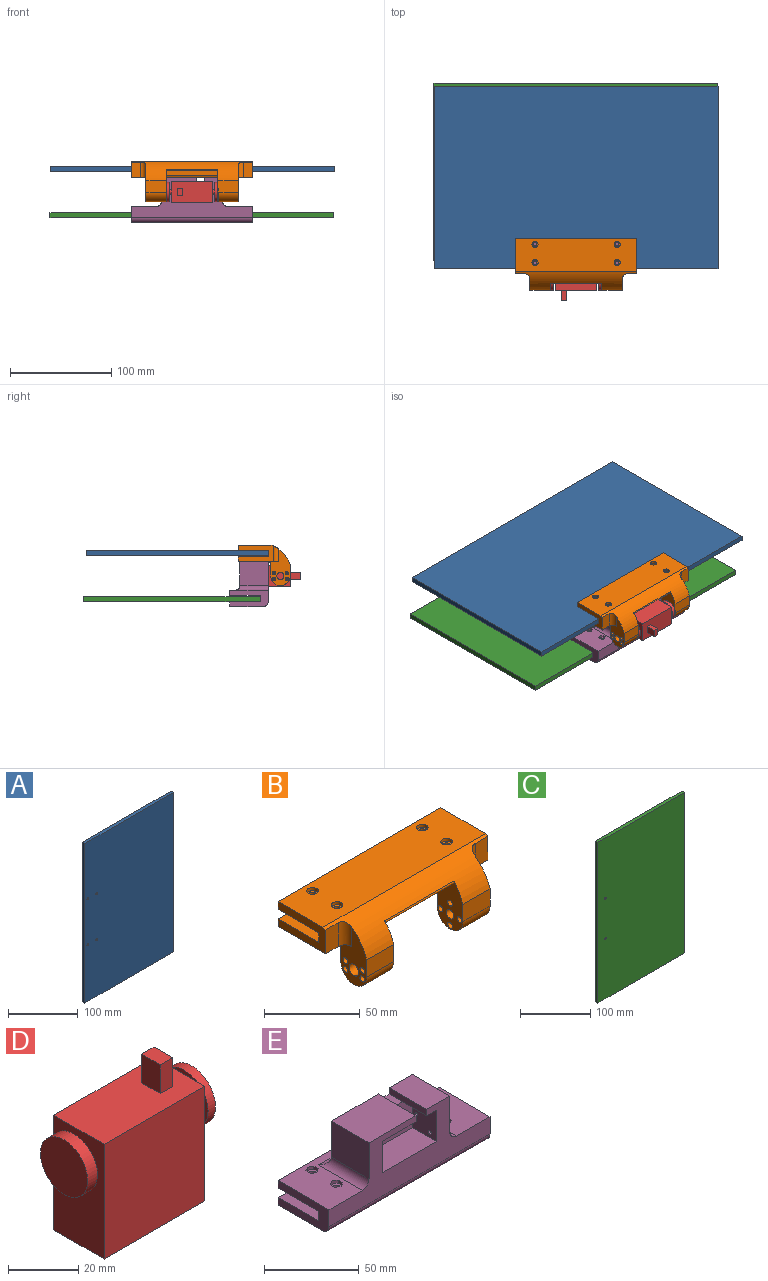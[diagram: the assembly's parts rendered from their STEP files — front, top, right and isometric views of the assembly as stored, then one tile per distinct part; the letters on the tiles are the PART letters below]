
ASSEMBLY  parts=5 mates=12
PART A: 10 faces, bbox 180x5x280 mm
  f0: plane 280x5mm, normal (1,0,0), area 1400mm2, adj f1,f6,f8,f9
  f1: plane 180x5mm, normal (0,0,1), area 900mm2, adj f0,f2,f8,f9
  f2: plane 280x5mm, normal (-1,0,0), area 1400mm2, adj f1,f6,f8,f9
  f3: cylinder r=1.75mm len=5mm, axis (0,1,0), area 55mm2, adj f8,f9
  f4: cylinder r=1.75mm len=5mm, axis (0,1,0), area 55mm2, adj f8,f9
  f5: cylinder r=1.75mm len=5mm, axis (0,1,0), area 55mm2, adj f8,f9
  f6: plane 180x5mm, normal (0,0,-1), area 900mm2, adj f0,f2,f8,f9
  f7: cylinder r=1.75mm len=5mm, axis (0,1,0), area 55mm2, adj f8,f9
  f8: plane 280x180mm, normal (0,-1,0), area 50361.5mm2, adj f0,f1,f2,f3,f4,f5,f6,f7
  f9: plane 280x180mm, normal (0,1,0), area 50361.5mm2, adj f0,f1,f2,f3,f4,f5,f6,f7
PART B: 92 faces, bbox 120x51x39.7 mm
  f0: plane 35.91x21mm, normal (-1,0,0), area 403.7mm2, adj f2,f12,f22,f28,f29,f33,f35,f37
  f1: plane 35.91x21mm, normal (1,0,0), area 418.5mm2, adj f2,f12,f21,f27,f30,f31,f42,f87
  f2: cylinder r=30mm len=120mm, axis (1,0,0), area 1848.5mm2, adj f0,f1,f11,f18,f19,f21,f28,f44
  f3: cylinder r=1.75mm len=3.5mm, axis (0,0,1), area 31.9mm2, adj f14,f76
  f4: cylinder r=1.75mm len=3.5mm, axis (0,0,1), area 31.9mm2, adj f14,f69
  f5: cylinder r=1.75mm len=3.5mm, axis (0,0,1), area 31.9mm2, adj f14,f68
  f6: cylinder r=1.75mm len=3.5mm, axis (0,0,1), area 31.9mm2, adj f14,f61
  f7: cylinder r=1.75mm len=3.5mm, axis (0,0,1), area 33mm2, adj f13,f53
  f8: cylinder r=1.75mm len=3.5mm, axis (0,0,1), area 33mm2, adj f13,f51
  f9: cylinder r=1.75mm len=3.5mm, axis (0,0,1), area 33mm2, adj f13,f50
  f10: cylinder r=1.75mm len=3.5mm, axis (0,0,1), area 33mm2, adj f13,f48
  f11: plane 120x33.17mm, normal (0,0,1), area 3867.3mm2, adj f2,f17,f44,f45,f47,f49,f52,f54
  f12: plane 120x40mm, normal (0,0,-1), area 3631mm2, adj f0,f1,f16,f42,f43,f44,f45,f55
  f13: plane 120x30mm, normal (0,0,-1), area 3561.5mm2, adj f7,f8,f9,f10,f15,f17,f44,f45
  f14: plane 120x30mm, normal (0,0,1), area 3561.5mm2, adj f3,f4,f5,f6,f15,f16,f44,f45
  f15: plane 120x6.1mm, normal (0,1,0), area 732mm2, adj f13,f14,f44,f45
  f16: plane 120x4.9mm, normal (0,1,0), area 588mm2, adj f12,f14,f44,f45
  f17: plane 120x5mm, normal (0,1,0), area 600mm2, adj f11,f13,f44,f45
  f18: plane 32.08x21mm, normal (1,0,0), area 467.1mm2, adj f2,f20,f22,f23,f24,f25,f26,f28
  f19: plane 32.08x21mm, normal (-1,0,0), area 457.2mm2, adj f2,f20,f21,f27,f30,f31,f41,f42
  f20: plane 51x11.57mm, normal (0,0,-1), area 589.9mm2, adj f18,f19,f41,f46
  f21: plane 20x10.9mm, normal (0,-1,0), area 218mm2, adj f1,f2,f19,f30
  f22: plane 20x12.15mm, normal (0,1,0), area 243mm2, adj f0,f18,f29,f43
  f23: cylinder r=1.05mm len=2.1mm, axis (1,0,0), area 9.9mm2, adj f18,f38
  f24: cylinder r=1.05mm len=2.1mm, axis (1,0,0), area 9.9mm2, adj f18,f36
  f25: cylinder r=1.05mm len=2.1mm, axis (1,0,0), area 9.9mm2, adj f18,f34
  f26: cylinder r=1.05mm len=2.1mm, axis (1,0,0), area 9.9mm2, adj f18,f32
  f27: plane 20x12.15mm, normal (0,1,0), area 243mm2, adj f1,f19,f30,f42
  f28: plane 20x10.9mm, normal (0,-1,0), area 218mm2, adj f0,f2,f18,f29
  f29: cylinder r=9.5mm len=20mm, axis (1,0,0), area 596.9mm2, adj f0,f18,f22,f28
  f30: cylinder r=9.5mm len=20mm, axis (1,0,0), area 596.9mm2, adj f1,f19,f21,f27
  f31: cylinder r=2.75mm len=20mm, axis (1,0,0), area 345.6mm2, adj f1,f19
  f32: plane 3.5x3.5mm, normal (-1,0,0), area 6.2mm2, adj f26,f33
  f33: cylinder r=1.75mm len=18.5mm, axis (-1,0,0), area 203.4mm2, adj f0,f32
  f34: plane 3.5x3.5mm, normal (-1,0,0), area 6.2mm2, adj f25,f35
  f35: cylinder r=1.75mm len=18.5mm, axis (-1,0,0), area 203.4mm2, adj f0,f34
  f36: plane 3.5x3.5mm, normal (-1,0,0), area 6.2mm2, adj f24,f37
  f37: cylinder r=1.75mm len=18.5mm, axis (-1,0,0), area 203.4mm2, adj f0,f36
  f38: plane 3.5x3.5mm, normal (-1,0,0), area 6.2mm2, adj f23,f39
  f39: cylinder r=1.75mm len=18.5mm, axis (-1,0,0), area 203.4mm2, adj f0,f38
  f40: cylinder r=3.5mm len=20mm, axis (-1,0,0), area 439.8mm2, adj f0,f18
  f41: plane 51x4.75mm, normal (0,-1,0), area 242.3mm2, adj f18,f19,f20,f83
  f42: cylinder r=2mm len=20mm, axis (-1,0,0), area 62.8mm2, adj f1,f12,f19,f27
  f43: cylinder r=2mm len=20mm, axis (-1,0,0), area 62.8mm2, adj f0,f12,f18,f22
  f44: plane 35x16mm, normal (1,0,0), area 376.3mm2, adj f2,f11,f12,f13,f14,f15,f16,f17
  f45: plane 35x16mm, normal (-1,0,0), area 376.3mm2, adj f2,f11,f12,f13,f14,f15,f16,f17
  f46: cylinder r=1mm len=51mm, axis (1,0,0), area 118.2mm2, adj f2,f18,f19,f20
  f47: cylinder r=3mm len=6mm, axis (0,0,1), area 37.7mm2, adj f11,f48
  f48: plane 6x6mm, normal (0,0,1), area 18.7mm2, adj f10,f47
  f49: cylinder r=3mm len=6mm, axis (0,0,1), area 37.7mm2, adj f11,f50
  f50: plane 6x6mm, normal (0,0,1), area 18.7mm2, adj f9,f49
  f51: plane 6x6mm, normal (0,0,1), area 18.7mm2, adj f8,f52
  f52: cylinder r=3mm len=6mm, axis (0,0,1), area 37.7mm2, adj f11,f51
  f53: plane 6x6mm, normal (0,0,1), area 18.7mm2, adj f7,f54
  f54: cylinder r=3mm len=6mm, axis (0,0,1), area 37.7mm2, adj f11,f53
  f55: plane 3x2mm, normal (-0.5,-0.87,0), area 6.9mm2, adj f12,f56,f60,f61
  f56: plane 3.46x2mm, normal (-1,0,0), area 6.9mm2, adj f12,f55,f57,f61
  f57: plane 3x2mm, normal (-0.5,0.87,0), area 6.9mm2, adj f12,f56,f58,f61
  f58: plane 3x2mm, normal (0.5,0.87,0), area 6.9mm2, adj f12,f57,f59,f61
  f59: plane 3.46x2mm, normal (1,0,0), area 6.9mm2, adj f12,f58,f60,f61
  f60: plane 3x2mm, normal (0.5,-0.87,0), area 6.9mm2, adj f12,f55,f59,f61
  f61: plane 6.93x6mm, normal (0,0,-1), area 21.6mm2, adj f6,f55,f56,f57,f58,f59,f60
  f62: plane 3x2mm, normal (-0.5,-0.87,0), area 6.9mm2, adj f12,f63,f67,f68
  f63: plane 3.46x2mm, normal (-1,0,0), area 6.9mm2, adj f12,f62,f64,f68
  f64: plane 3x2mm, normal (-0.5,0.87,0), area 6.9mm2, adj f12,f63,f65,f68
  f65: plane 3x2mm, normal (0.5,0.87,0), area 6.9mm2, adj f12,f64,f66,f68
  f66: plane 3.46x2mm, normal (1,0,0), area 6.9mm2, adj f12,f65,f67,f68
  f67: plane 3x2mm, normal (0.5,-0.87,0), area 6.9mm2, adj f12,f62,f66,f68
  f68: plane 6.93x6mm, normal (0,0,-1), area 21.6mm2, adj f5,f62,f63,f64,f65,f66,f67
  f69: plane 6.93x6mm, normal (0,0,-1), area 21.6mm2, adj f4,f70,f71,f72,f73,f74,f75
  f70: plane 3x2mm, normal (-0.5,-0.87,0), area 6.9mm2, adj f12,f69,f71,f75
  f71: plane 3.46x2mm, normal (-1,0,0), area 6.9mm2, adj f12,f69,f70,f72
  f72: plane 3x2mm, normal (-0.5,0.87,0), area 6.9mm2, adj f12,f69,f71,f73
  f73: plane 3x2mm, normal (0.5,0.87,0), area 6.9mm2, adj f12,f69,f72,f74
  f74: plane 3.46x2mm, normal (1,0,0), area 6.9mm2, adj f12,f69,f73,f75
  f75: plane 3x2mm, normal (0.5,-0.87,0), area 6.9mm2, adj f12,f69,f70,f74
  f76: plane 6.93x6mm, normal (0,0,-1), area 21.6mm2, adj f3,f77,f78,f79,f80,f81,f82
  f77: plane 3x2mm, normal (-0.5,-0.87,0), area 6.9mm2, adj f12,f76,f78,f82
  f78: plane 3.46x2mm, normal (-1,0,0), area 6.9mm2, adj f12,f76,f77,f79
  f79: plane 3x2mm, normal (-0.5,0.87,0), area 6.9mm2, adj f12,f76,f78,f80
  f80: plane 3x2mm, normal (0.5,0.87,0), area 6.9mm2, adj f12,f76,f79,f81
  f81: plane 3.46x2mm, normal (1,0,0), area 6.9mm2, adj f12,f76,f80,f82
  f82: plane 3x2mm, normal (0.5,-0.87,0), area 6.9mm2, adj f12,f76,f77,f81
  f83: cylinder r=2mm len=51mm, axis (-1,0,0), area 160.2mm2, adj f12,f18,f19,f41
  f84: plane 15.22x9.5mm, normal (0,-1,0), area 144.6mm2, adj f2,f12,f44,f87
  f85: plane 15.22x9.5mm, normal (0,-1,0), area 144.6mm2, adj f2,f12,f45,f86
  f86: cylinder r=5mm len=15.22mm, axis (0,0,1), area 111.8mm2, adj f0,f2,f12,f85
  f87: cylinder r=5mm len=15.22mm, axis (0,0,-1), area 111.8mm2, adj f1,f2,f12,f84
  f88: cylinder r=1.75mm len=20mm, axis (1,0,0), area 219.9mm2, adj f1,f19
  f89: cylinder r=1.75mm len=20mm, axis (1,0,0), area 219.9mm2, adj f1,f19
  f90: cylinder r=1.75mm len=20mm, axis (1,0,0), area 219.9mm2, adj f1,f19
  f91: cylinder r=1.75mm len=20mm, axis (1,0,0), area 219.9mm2, adj f1,f19
PART C: 8 faces, bbox 174.5x5x280 mm
  f0: plane 280x5mm, normal (1,0,0), area 1400mm2, adj f1,f4,f6,f7
  f1: plane 174.5x5mm, normal (0,0,1), area 872.5mm2, adj f0,f2,f6,f7
  f2: plane 280x5mm, normal (-1,0,0), area 1400mm2, adj f1,f4,f6,f7
  f3: cylinder r=1.5mm len=5mm, axis (0,1,0), area 47.1mm2, adj f6,f7
  f4: plane 174.5x5mm, normal (0,0,-1), area 872.5mm2, adj f0,f2,f6,f7
  f5: cylinder r=1.5mm len=5mm, axis (0,1,0), area 47.1mm2, adj f6,f7
  f6: plane 280x174.5mm, normal (0,-1,0), area 48845.9mm2, adj f0,f1,f2,f3,f4,f5
  f7: plane 280x174.5mm, normal (0,1,0), area 48845.9mm2, adj f0,f1,f2,f3,f4,f5
PART D: 19 faces, bbox 51.5x20.3x50 mm
  f0: plane 40.5x20.3mm, normal (0,0,1), area 784.7mm2, adj f1,f3,f4,f5,f14,f15,f16,f17
  f1: plane 40x20.3mm, normal (-1,0,0), area 792.4mm2, adj f0,f2,f4,f5,f6
  f2: plane 40.5x20.3mm, normal (0,0,-1), area 822.2mm2, adj f1,f3,f4,f5
  f3: plane 40x20.3mm, normal (1,0,0), area 792.4mm2, adj f0,f2,f4,f5,f7
  f4: plane 40.5x40mm, normal (0,-1,0), area 1620mm2, adj f0,f1,f2,f3
  f5: plane 40.5x40mm, normal (0,1,0), area 1620mm2, adj f0,f1,f2,f3
  f6: cylinder r=2.5mm len=5mm, axis (1,0,0), area 31.4mm2, adj f1,f10
  f7: cylinder r=2.5mm len=5mm, axis (-1,0,0), area 31.4mm2, adj f3,f13
  f8: cylinder r=9.5mm len=19mm, axis (1,0,0), area 238.8mm2, adj f9,f10
  f9: plane 19x19mm, normal (-1,0,0), area 283.5mm2, adj f8
  f10: plane 19x19mm, normal (1,0,0), area 263.9mm2, adj f6,f8
  f11: cylinder r=9.5mm len=19mm, axis (-1,0,0), area 179.1mm2, adj f12,f13
  f12: plane 19x19mm, normal (1,0,0), area 283.5mm2, adj f11
  f13: plane 19x19mm, normal (-1,0,0), area 263.9mm2, adj f7,f11
  f14: plane 10x5mm, normal (0,1,0), area 50mm2, adj f0,f15,f17,f18
  f15: plane 10x7.5mm, normal (-1,0,0), area 75mm2, adj f0,f14,f16,f18
  f16: plane 10x5mm, normal (0,-1,0), area 50mm2, adj f0,f15,f17,f18
  f17: plane 10x7.5mm, normal (1,0,0), area 75mm2, adj f0,f14,f16,f18
  f18: plane 7.5x5mm, normal (0,0,1), area 37.5mm2, adj f14,f15,f16,f17
PART E: 81 faces, bbox 120x38x44.3 mm
  f0: cylinder r=1.75mm len=3.5mm, axis (0,0,1), area 33mm2, adj f15,f71
  f1: cylinder r=1.75mm len=3.5mm, axis (0,0,1), area 33mm2, adj f15,f64
  f2: cylinder r=1.75mm len=3.5mm, axis (0,0,1), area 33mm2, adj f15,f63
  f3: cylinder r=1.75mm len=3.5mm, axis (0,0,1), area 33mm2, adj f15,f56
  f4: cylinder r=1.75mm len=3.5mm, axis (0,0,1), area 31.9mm2, adj f12,f48
  f5: cylinder r=1.75mm len=3.5mm, axis (0,0,1), area 31.9mm2, adj f12,f46
  f6: cylinder r=1.75mm len=3.5mm, axis (0,0,1), area 31.9mm2, adj f12,f45
  f7: cylinder r=1.75mm len=3.5mm, axis (0,0,1), area 31.9mm2, adj f12,f43
  f8: plane 120x33mm, normal (0,0,-1), area 3846.9mm2, adj f11,f39,f40,f41,f42,f44,f47,f49
  f9: plane 120x39.3mm, normal (0,-1,0), area 2187.1mm2, adj f10,f19,f20,f22,f23,f24,f25,f26
  f10: plane 120x38mm, normal (0,0,1), area 2115.4mm2, adj f9,f14,f39,f40,f50,f51,f52,f53
  f11: plane 120x4.9mm, normal (0,1,0), area 588mm2, adj f8,f12,f39,f40
  f12: plane 120x30mm, normal (0,0,1), area 3561.5mm2, adj f4,f5,f6,f7,f11,f13,f39,f40
  f13: plane 120x6.1mm, normal (0,1,0), area 732mm2, adj f12,f15,f39,f40
  f14: plane 120x5mm, normal (0,1,0), area 600mm2, adj f10,f15,f39,f40
  f15: plane 120x30mm, normal (0,0,-1), area 3561.5mm2, adj f0,f1,f2,f3,f13,f14,f39,f40
  f16: cylinder r=1.05mm len=2.1mm, axis (1,0,0), area 9.9mm2, adj f29,f37
  f17: cylinder r=1.05mm len=2.1mm, axis (1,0,0), area 9.9mm2, adj f29,f35
  f18: cylinder r=1.05mm len=2.1mm, axis (1,0,0), area 9.9mm2, adj f29,f33
  f19: plane 28x23.3mm, normal (-1,0,0), area 652.4mm2, adj f9,f21,f25,f78
  f20: plane 28x23.3mm, normal (1,0,0), area 623.5mm2, adj f9,f21,f26,f34,f36,f38,f79
  f21: plane 60.3x23.3mm, normal (0,1,0), area 1373mm2, adj f19,f20,f24,f25,f26,f27,f32,f80
  f22: plane 20.3x18mm, normal (1,0,0), area 365.4mm2, adj f9,f23,f30,f31
  f23: plane 25x18mm, normal (0,0,-1), area 450mm2, adj f9,f22,f24,f31
  f24: plane 28x4mm, normal (1,0,0), area 112mm2, adj f9,f21,f23,f25,f32
  f25: plane 35x28mm, normal (0,0,1), area 980mm2, adj f9,f19,f21,f24
  f26: plane 28x17.3mm, normal (0,0,1), area 484.4mm2, adj f9,f20,f21,f27
  f27: plane 28x4mm, normal (-1,0,0), area 112mm2, adj f9,f21,f26,f28,f32
  f28: plane 18x7.3mm, normal (0,0,-1), area 131.4mm2, adj f9,f27,f29,f31
  f29: plane 20.3x18mm, normal (-1,0,0), area 355mm2, adj f9,f16,f17,f18,f28,f30,f31
  f30: plane 40.3x18mm, normal (0,0,1), area 725.4mm2, adj f9,f22,f29,f31
  f31: plane 40.3x20.3mm, normal (0,-1,0), area 818.1mm2, adj f22,f23,f28,f29,f30,f32
  f32: plane 10x8mm, normal (0,0,1), area 80mm2, adj f21,f24,f27,f31
  f33: plane 3.5x3.5mm, normal (1,0,0), area 6.2mm2, adj f18,f34
  f34: cylinder r=1.75mm len=8.5mm, axis (1,0,0), area 93.5mm2, adj f20,f33
  f35: plane 3.5x3.5mm, normal (1,0,0), area 6.2mm2, adj f17,f36
  f36: cylinder r=1.75mm len=8.5mm, axis (1,0,0), area 93.5mm2, adj f20,f35
  f37: plane 3.5x3.5mm, normal (1,0,0), area 6.2mm2, adj f16,f38
  f38: cylinder r=1.75mm len=8.5mm, axis (1,0,0), area 93.5mm2, adj f20,f37
  f39: plane 38x16mm, normal (-1,0,0), area 419.6mm2, adj f8,f9,f10,f11,f12,f13,f14,f15
  f40: plane 38x16mm, normal (1,0,0), area 419.6mm2, adj f8,f9,f10,f11,f12,f13,f14,f15
  f41: cylinder r=5mm len=120mm, axis (-1,0,0), area 942.5mm2, adj f8,f9,f39,f40
  f42: cylinder r=3mm len=6mm, axis (0,0,-1), area 37.7mm2, adj f8,f43
  f43: plane 6x6mm, normal (0,0,-1), area 18.7mm2, adj f7,f42
  f44: cylinder r=3mm len=6mm, axis (0,0,-1), area 37.7mm2, adj f8,f45
  f45: plane 6x6mm, normal (0,0,-1), area 18.7mm2, adj f6,f44
  f46: plane 6x6mm, normal (0,0,-1), area 18.7mm2, adj f5,f47
  f47: cylinder r=3mm len=6mm, axis (0,0,-1), area 37.7mm2, adj f8,f46
  f48: plane 6x6mm, normal (0,0,-1), area 18.7mm2, adj f4,f49
  f49: cylinder r=3mm len=6mm, axis (0,0,-1), area 37.7mm2, adj f8,f48
  f50: plane 3x2mm, normal (0.5,-0.87,0), area 6.9mm2, adj f10,f51,f55,f56
  f51: plane 3.46x2mm, normal (1,0,0), area 6.9mm2, adj f10,f50,f52,f56
  f52: plane 3x2mm, normal (0.5,0.87,0), area 6.9mm2, adj f10,f51,f53,f56
  f53: plane 3x2mm, normal (-0.5,0.87,0), area 6.9mm2, adj f10,f52,f54,f56
  f54: plane 3.46x2mm, normal (-1,0,0), area 6.9mm2, adj f10,f53,f55,f56
  f55: plane 3x2mm, normal (-0.5,-0.87,0), area 6.9mm2, adj f10,f50,f54,f56
  f56: plane 6.93x6mm, normal (0,0,1), area 21.6mm2, adj f3,f50,f51,f52,f53,f54,f55
  f57: plane 3x2mm, normal (-0.5,0.87,0), area 6.9mm2, adj f10,f58,f62,f63
  f58: plane 3.46x2mm, normal (-1,0,0), area 6.9mm2, adj f10,f57,f59,f63
  f59: plane 3x2mm, normal (-0.5,-0.87,0), area 6.9mm2, adj f10,f58,f60,f63
  f60: plane 3x2mm, normal (0.5,-0.87,0), area 6.9mm2, adj f10,f59,f61,f63
  f61: plane 3.46x2mm, normal (1,0,0), area 6.9mm2, adj f10,f60,f62,f63
  f62: plane 3x2mm, normal (0.5,0.87,0), area 6.9mm2, adj f10,f57,f61,f63
  f63: plane 6.93x6mm, normal (0,0,1), area 21.6mm2, adj f2,f57,f58,f59,f60,f61,f62
  f64: plane 6.93x6mm, normal (0,0,1), area 21.6mm2, adj f1,f65,f66,f67,f68,f69,f70
  f65: plane 3x2mm, normal (0.5,-0.87,0), area 6.9mm2, adj f10,f64,f66,f70
  f66: plane 3.46x2mm, normal (1,0,0), area 6.9mm2, adj f10,f64,f65,f67
  f67: plane 3x2mm, normal (0.5,0.87,0), area 6.9mm2, adj f10,f64,f66,f68
  f68: plane 3x2mm, normal (-0.5,0.87,0), area 6.9mm2, adj f10,f64,f67,f69
  f69: plane 3.46x2mm, normal (-1,0,0), area 6.9mm2, adj f10,f64,f68,f70
  f70: plane 3x2mm, normal (-0.5,-0.87,0), area 6.9mm2, adj f10,f64,f65,f69
  f71: plane 6.93x6mm, normal (0,0,1), area 21.6mm2, adj f0,f72,f73,f74,f75,f76,f77
  f72: plane 3x2mm, normal (-0.5,0.87,0), area 6.9mm2, adj f10,f71,f73,f77
  f73: plane 3.46x2mm, normal (-1,0,0), area 6.9mm2, adj f10,f71,f72,f74
  f74: plane 3x2mm, normal (-0.5,-0.87,0), area 6.9mm2, adj f10,f71,f73,f75
  f75: plane 3x2mm, normal (0.5,-0.87,0), area 6.9mm2, adj f10,f71,f74,f76
  f76: plane 3.46x2mm, normal (1,0,0), area 6.9mm2, adj f10,f71,f75,f77
  f77: plane 3x2mm, normal (0.5,0.87,0), area 6.9mm2, adj f10,f71,f72,f76
  f78: cylinder r=5mm len=33mm, axis (0,-1,0), area 234.2mm2, adj f9,f10,f19,f80
  f79: cylinder r=5mm len=33mm, axis (0,1,0), area 234.2mm2, adj f9,f10,f20,f80
  f80: cylinder r=5mm len=70.3mm, axis (1,0,0), area 502.1mm2, adj f10,f21,f78,f79
PLACE A rot(axis=(-0.58,-0.58,0.58),120deg) t=(-61,47.58,-21.27)mm
PLACE B t=(-86.5,-44.42,-50.92)mm
PLACE C rot(axis=(-0.58,-0.58,0.58),120deg) t=(-61.15,53.33,-66.67)mm
PLACE D rot(axis=(0,-0.71,0.71),180deg) t=(-41,-23.92,-51.57)mm
PLACE E t=(-61.15,-23.92,-41.42)mm fixed
MATE planar D.f5 <-> E.f30  axis (0,0,-1) through (-61.25,-43.92,-51.57)mm
MATE cylindrical C.f3 <-> E.f1  axis (0,0,-1) through (-96.65,-18.92,-64.17)mm
MATE planar D.f1 <-> E.f29  axis (1,0,0) through (-41,-43.67,-41.42)mm
MATE parallel A.f8 <-> C.f6  axis (0,0,1) through (-61,47.64,-16.27)mm
MATE cylindrical D.f7 <-> B.f29  axis (1,0,0) through (-85,-53.92,-41.42)mm
MATE planar C.f7 <-> E.f12  axis (0,0,-1) through (-61.15,53.35,-66.67)mm
MATE planar D.f2 <-> E.f31  axis (0,1,0) through (-61.25,-23.92,-41.42)mm
MATE cylindrical A.f3 <-> B.f49  axis (0,0,-1) through (-20.5,-18.42,-21.27)mm
MATE cylindrical A.f5 <-> B.f54  axis (0,0,-1) through (-101.5,-36.42,-18.77)mm
MATE planar B.f13 <-> A.f8  axis (0,0,-1) through (-61,-27.42,-16.27)mm
MATE planar B.f18 <-> D.f7  axis (1,0,0) through (-86.5,-53.52,-34.5)mm
MATE cylindrical C.f5 <-> E.f0  axis (0,0,-1) through (-25.65,-18.92,-61.67)mm
